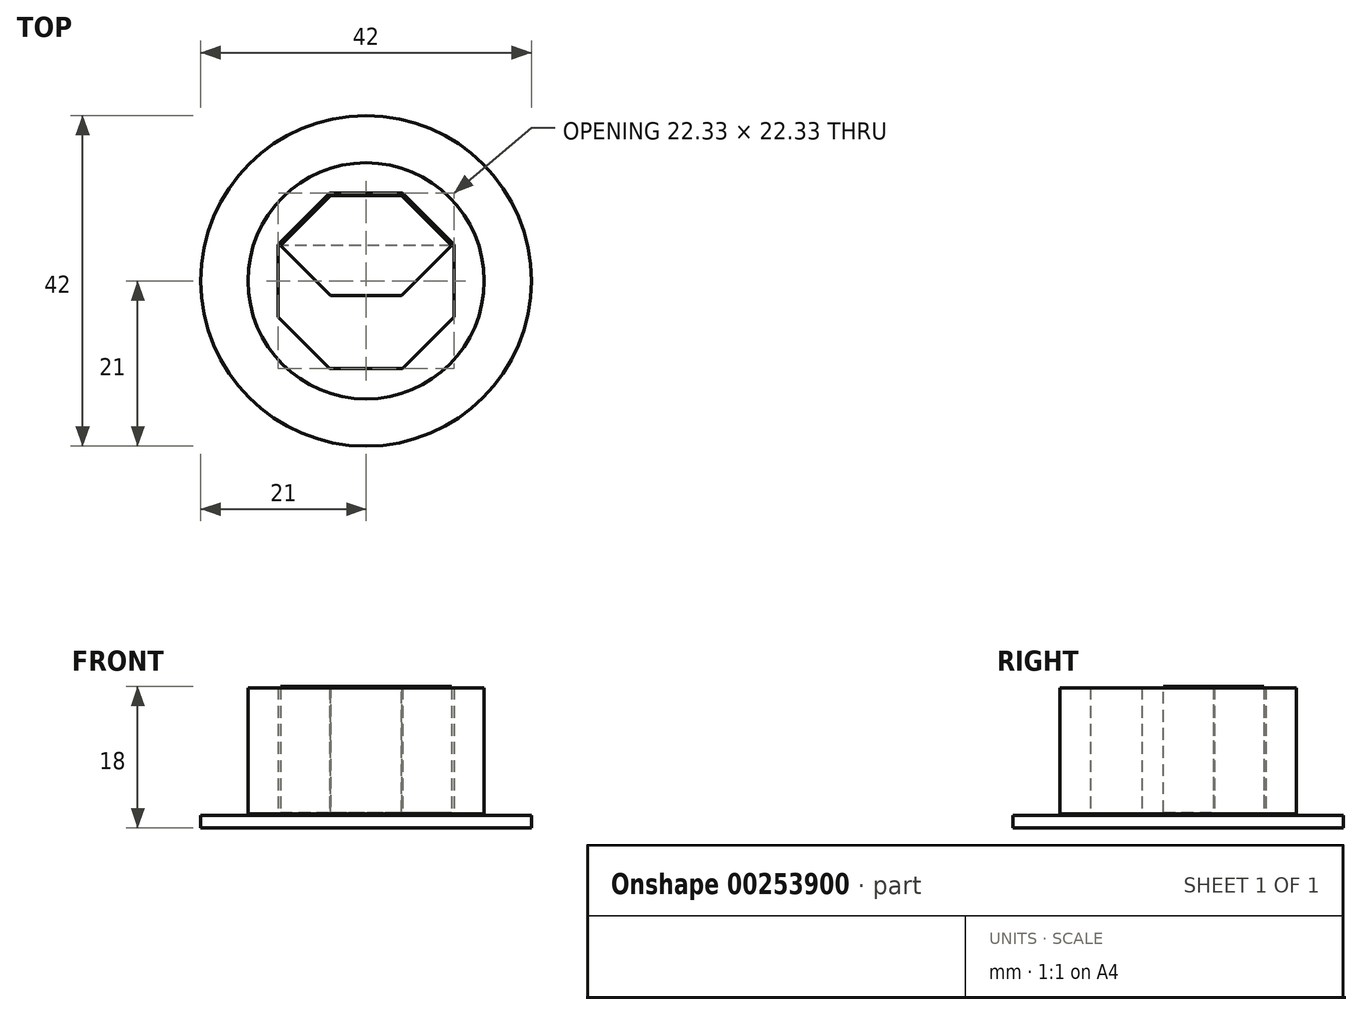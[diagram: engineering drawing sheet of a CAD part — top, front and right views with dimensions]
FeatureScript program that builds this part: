
annotation { "Feature Type Name" : "Feature", "Feature Type Description" : "" }
export const myFeature = defineFeature(function(context is Context, id is Id, definition is map)
    precondition{}
    {
        {
            var Q0;
            Q0=qCreatedBy(makeId("Top.planeOp"),FACE);
            var sketch = newSketch(context, id + "F0", { "sketchPlane" : qUnion([Q0])});
            skCircle(sketch, "E0", {"center": v(0, 0) * mm, "radius": 21 * mm});
            skSolve(sketch);
        }
        {
            var Q0;
            Q0 = qSketchRegion(id + "F0", true);
            extrude(context, id + "F1", {"entities" : qUnion([Q0]), "depth" : 1.6 * mm});
        }
        {
            var Q0;
            Q0=makeQuery(id+"F1.opExtrude","CAP_FACE",FACE,{"disambiguationData":[OSD([sQuery(id+"F0.wireOp",EDGE,"E0")])],"isStart":false});
            var sketch = newSketch(context, id + "F2", { "sketchPlane" : qUnion([Q0])});
            skCircle(sketch, "E1.cCircle", {"center": v(0, 0) * mm, "radius": 10.86 * mm, "construction": true});
            skLineSegment(sketch, "E1.0", {"start": v(10.86, 4.5) * mm, "end": v(10.86, -4.5) * mm});
            skLineSegment(sketch, "E1.1", {"start": v(10.86, -4.5) * mm, "end": v(4.5, -10.86) * mm});
            skLineSegment(sketch, "E1.2", {"start": v(4.5, -10.86) * mm, "end": v(-4.5, -10.86) * mm});
            skLineSegment(sketch, "E1.3", {"start": v(-4.5, -10.86) * mm, "end": v(-10.86, -4.5) * mm});
            skLineSegment(sketch, "E1.4", {"start": v(-10.86, -4.5) * mm, "end": v(-10.86, 4.5) * mm});
            skLineSegment(sketch, "E1.5", {"start": v(-10.86, 4.5) * mm, "end": v(-4.5, 10.86) * mm});
            skLineSegment(sketch, "E1.6", {"start": v(-4.5, 10.86) * mm, "end": v(4.5, 10.86) * mm});
            skLineSegment(sketch, "E1.7", {"start": v(4.5, 10.86) * mm, "end": v(10.86, 4.5) * mm});
            skPoint(sketch, "E1.0.midPoint", {"position": v(10.86, 0) * mm});
            skSolve(sketch);
        }
        {
            var Q0;
            Q0 = qSketchRegion(id + "F2", true);
            extrude(context, id + "F3", {"entities" : qUnion([Q0]), "operationType" : NewBodyOperationType.ADD, "depth" : 16.4 * mm});
        }
        {
            var Q0;
            Q0=makeQuery(id+"F1.opExtrude","CAP_FACE",FACE,{"disambiguationData":[OSD([sQuery(id+"F0.wireOp",EDGE,"E0")])],"isStart":false});
            var sketch = newSketch(context, id + "F4", { "sketchPlane" : qUnion([Q0])});
            skCircle(sketch, "E2", {"center": v(0, 0) * mm, "radius": 15 * mm});
            skCircle(sketch, "E3", {"center": v(0, 0) * mm, "radius": 13.8 * mm});
            skCircle(sketch, "E4.cCircle", {"center": v(0, 0) * mm, "radius": 11.16 * mm, "construction": true});
            skLineSegment(sketch, "E4.0", {"start": v(-4.62, 11.16) * mm, "end": v(4.62, 11.16) * mm});
            skLineSegment(sketch, "E4.1", {"start": v(4.62, 11.16) * mm, "end": v(11.16, 4.62) * mm});
            skLineSegment(sketch, "E4.2", {"start": v(11.16, 4.62) * mm, "end": v(11.16, -4.62) * mm});
            skLineSegment(sketch, "E4.3", {"start": v(11.16, -4.62) * mm, "end": v(4.62, -11.16) * mm});
            skLineSegment(sketch, "E4.4", {"start": v(4.62, -11.16) * mm, "end": v(-4.62, -11.16) * mm});
            skLineSegment(sketch, "E4.5", {"start": v(-4.62, -11.16) * mm, "end": v(-11.16, -4.62) * mm});
            skLineSegment(sketch, "E4.6", {"start": v(-11.16, -4.62) * mm, "end": v(-11.16, 4.62) * mm});
            skLineSegment(sketch, "E4.7", {"start": v(-11.16, 4.62) * mm, "end": v(-4.62, 11.16) * mm});
            skPoint(sketch, "E4.0.midPoint", {"position": v(0, 11.16) * mm});
            skSolve(sketch);
        }
        {
            var Q0;
            Q0 = qSketchRegion(id + "F4", true);
            var Q1;
            Q1=makeQuery(id+"F4.imprint","IMPRINT",FACE,{"disambiguationData":[TD([[makeQuery(id+"F4.imprint","IMPRINT",EDGE,{"derivedFrom":sQuery(id+"F4.wireOp",EDGE,"E3")}),1.0]])]});
            extrude(context, id + "F5", {"entities" : qUnion([Q0, Q1]), "depth" : 16.2 * mm, "hasSecondDirection" : true, "secondDirectionOppositeDirection" : false, "secondDirectionDepth" : 0.2 * mm});
        }
        {
            var Q0;
            Q0=makeQuery(id+"F3.opExtrude","CAP_FACE",FACE,{"disambiguationData":[OSD([sQuery(id+"F2.wireOp",EDGE,"E1.0"),sQuery(id+"F2.wireOp",EDGE,"E1.1"),sQuery(id+"F2.wireOp",EDGE,"E1.2"),sQuery(id+"F2.wireOp",EDGE,"E1.3"),sQuery(id+"F2.wireOp",EDGE,"E1.4"),sQuery(id+"F2.wireOp",EDGE,"E1.5"),sQuery(id+"F2.wireOp",EDGE,"E1.6"),sQuery(id+"F2.wireOp",EDGE,"E1.7")])],"isStart":false});
            var sketch = newSketch(context, id + "F6", { "sketchPlane" : qUnion([Q0])});
            skLineSegment(sketch, "E5", {"start": v(-10.86, 4.5) * mm, "end": v(10.86, 4.5) * mm});
            skLineSegment(sketch, "E6.0.0", {"start": v(10.86, 4.5) * mm, "end": v(4.5, 10.86) * mm});
            skLineSegment(sketch, "E6.0.1", {"start": v(4.5, 10.86) * mm, "end": v(-4.5, 10.86) * mm});
            skLineSegment(sketch, "E6.0.2", {"start": v(-4.5, 10.86) * mm, "end": v(-10.86, 4.5) * mm});
            skLineSegment(sketch, "E6.0.3", {"start": v(-10.86, 4.5) * mm, "end": v(-10.86, -4.5) * mm});
            skLineSegment(sketch, "E6.0.4", {"start": v(-10.86, -4.5) * mm, "end": v(-4.5, -10.86) * mm});
            skLineSegment(sketch, "E6.0.5", {"start": v(-4.5, -10.86) * mm, "end": v(4.5, -10.86) * mm});
            skLineSegment(sketch, "E6.0.6", {"start": v(4.5, -10.86) * mm, "end": v(10.86, -4.5) * mm});
            skLineSegment(sketch, "E6.0.7", {"start": v(10.86, -4.5) * mm, "end": v(10.86, 4.5) * mm});
            skSolve(sketch);
        }
        {
            var Q0;
            Q0=makeQuery(id+"F6.imprint","IMPRINT",FACE,{"disambiguationData":[TD([[makeQuery(id+"F6.imprint","IMPRINT",EDGE,{"derivedFrom":sQuery(id+"F6.wireOp",EDGE,"E5")}),-1.0]])]});
            var Q1;
            Q1=makeQuery(id+"F1.opExtrude","CAP_FACE",FACE,{"disambiguationData":[OSD([sQuery(id+"F0.wireOp",EDGE,"E0")])],"isStart":false});
            extrude(context, id + "F7", {"entities" : qUnion([Q0]), "operationType" : NewBodyOperationType.REMOVE, "endBound" : BoundingType.UP_TO_SURFACE, "oppositeDirection" : true, "endBoundEntityFace" : qUnion([Q1]), "depth" : 25 * mm});
        }
        {
            var Q0;
            Q0=makeQuery(id+"F3.opExtrude","CAP_FACE",FACE,{"disambiguationData":[OSD([sQuery(id+"F2.wireOp",EDGE,"E1.0"),sQuery(id+"F2.wireOp",EDGE,"E1.1"),sQuery(id+"F2.wireOp",EDGE,"E1.2"),sQuery(id+"F2.wireOp",EDGE,"E1.3"),sQuery(id+"F2.wireOp",EDGE,"E1.4"),sQuery(id+"F2.wireOp",EDGE,"E1.5"),sQuery(id+"F2.wireOp",EDGE,"E1.6"),sQuery(id+"F2.wireOp",EDGE,"E1.7")])],"isStart":false});
            var sketch = newSketch(context, id + "F8", { "sketchPlane" : qUnion([Q0])});
            skLineSegment(sketch, "E7", {"start": v(-10.86, 4.5) * mm, "end": v(0, -6.36) * mm});
            skLineSegment(sketch, "E8", {"start": v(0, -6.36) * mm, "end": v(10.86, 4.5) * mm});
            skLineSegment(sketch, "E9", {"start": v(10.86, 4.5) * mm, "end": v(-10.86, 4.5) * mm});
            skLineSegment(sketch, "E10", {"start": v(-4.5, 10.86) * mm, "end": v(-4.5, -1.86) * mm});
            skLineSegment(sketch, "E11", {"start": v(-4.5, -1.86) * mm, "end": v(4.5, -1.86) * mm});
            skSolve(sketch);
        }
        {
            var Q0;
            {var subQ3=sQuery(id+"F8.wireOp",EDGE,"E11");Q0=makeQuery(id+"F8.imprint","IMPRINT",FACE,{"disambiguationData":[TD([[makeQuery(id+"F8.imprint","IMPRINT",EDGE,{"derivedFrom":subQ3}),1.0]])]});}
            var Q1;
            {var subQ0=sQuery(id+"F8.wireOp",EDGE,"E9");var subQ3=sQuery(id+"F8.wireOp",EDGE,"E10");var subQ5=makeQuery(id+"F8.imprint","INTERSECT",VERTEX,{"derivedFrom":[subQ0,subQ3]});Q1=makeQuery(id+"F8.imprint","IMPRINT",FACE,{"disambiguationData":[TD([[makeQuery(id+"F8.imprint","IMPRINT",EDGE,{"disambiguationData":[TD([[subQ5,1.0]])],"derivedFrom":subQ0}),-1.0]])]});}
            extrude(context, id + "F9", {"entities" : qUnion([Q0, Q1]), "operationType" : NewBodyOperationType.ADD, "oppositeDirection" : true, "depth" : 16 * mm});
        }
    });
